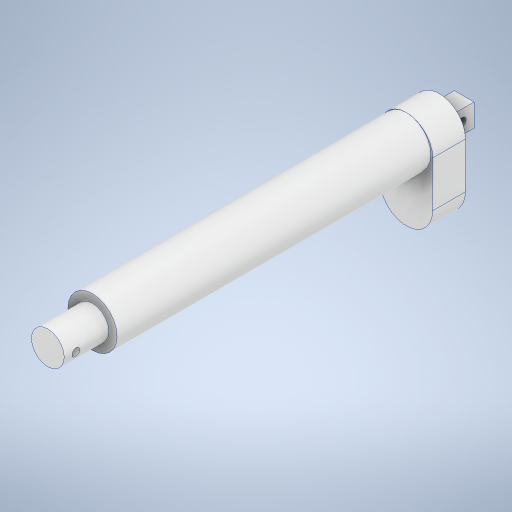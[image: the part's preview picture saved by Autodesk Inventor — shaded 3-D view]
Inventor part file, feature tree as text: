
AUTODESK INVENTOR PART (.ipt)
format: ipt  version: 2024 (Build 280153000, 153)  size: 287,744 bytes
history: native  units: mm
features: extrude x5, sketch x5, other x1
ambient origin geometry x8: Origin, YZ Plane, XZ Plane, XY Plane, X Axis, Y Axis, Z Axis, Center Point
bodies: Body1 (feature_tree)
feature tree (11):
  other  "솔리드1"
  extrude  "돌출1"  Depth=34.8mm
  extrude  "돌출2"  Depth=40.0mm
  extrude  "돌출3"  Depth=25.0mm TaperAngle=0.0deg
  extrude  "돌출4"  Depth=37.4mm
  extrude  "돌출5"  Depth=239.0mm TaperAngle=0.0deg
  sketch  "스케치1"
  sketch  "스케치2"
  sketch  "스케치3"
  sketch  "스케치5"
  sketch  "스케치6"
